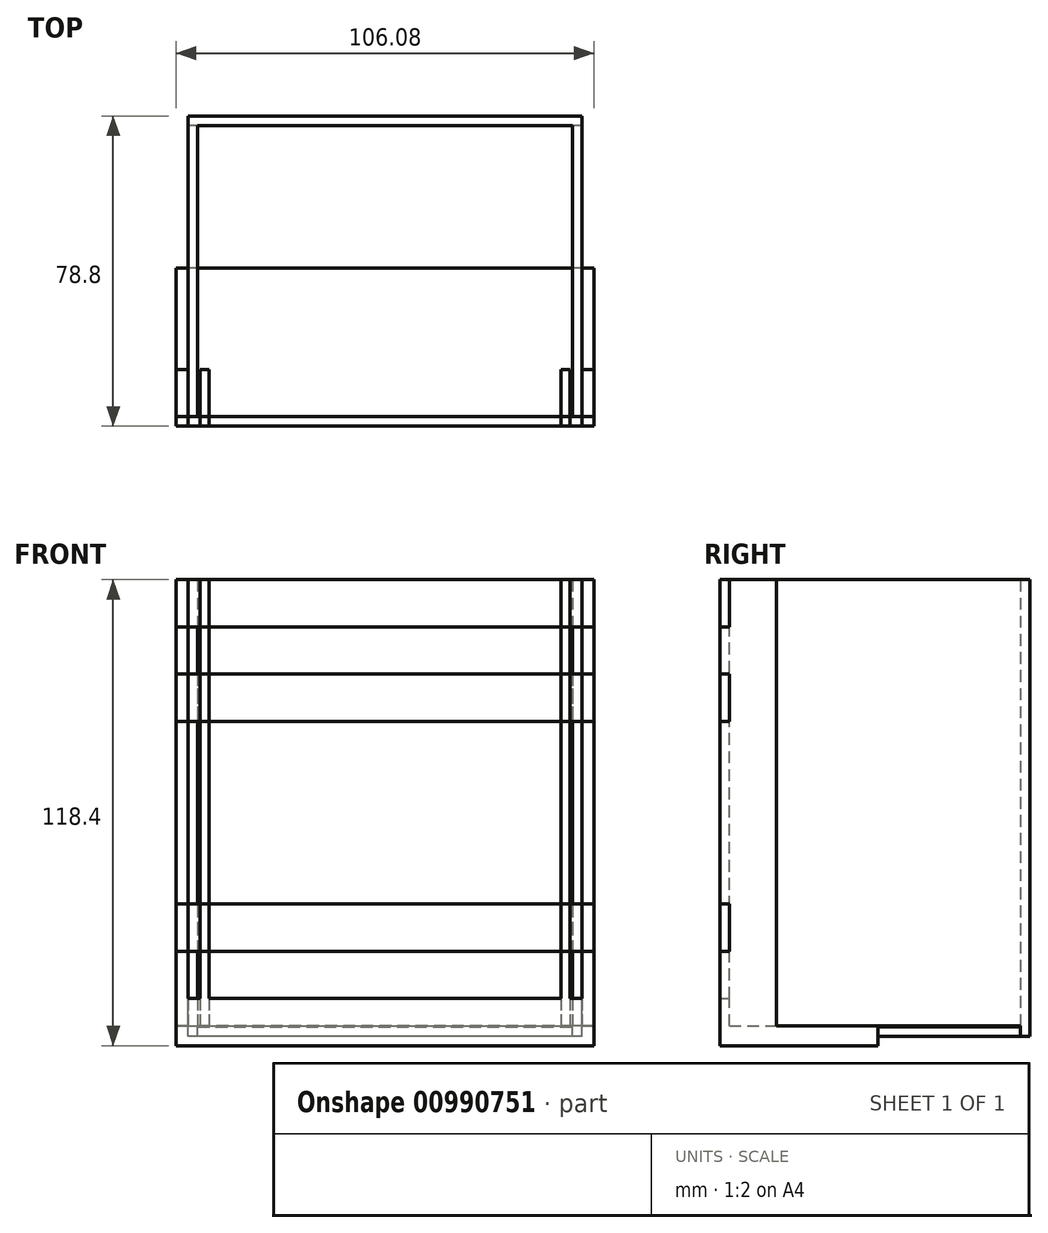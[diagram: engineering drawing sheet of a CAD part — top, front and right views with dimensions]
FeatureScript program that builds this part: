
annotation { "Feature Type Name" : "Feature", "Feature Type Description" : "" }
export const myFeature = defineFeature(function(context is Context, id is Id, definition is map)
    precondition{}
    {
        {
            var Q0;
            Q0=qCreatedBy(makeId("Front.planeOp"),FACE);
            var sketch = newSketch(context, id + "F0", { "sketchPlane" : qUnion([Q0])});
            skLineSegment(sketch, "E0.bottom", {"start": v(50, 0) * mm, "end": v(-50, 0) * mm});
            skLineSegment(sketch, "E0.top", {"start": v(50, 116) * mm, "end": v(-50, 116) * mm});
            skLineSegment(sketch, "E0.left", {"start": v(50, 0) * mm, "end": v(50, 116) * mm});
            skLineSegment(sketch, "E0.right", {"start": v(-50, 0) * mm, "end": v(-50, 116) * mm});
            skPoint(sketch, "E0.middle", {"position": v(0, 58) * mm});
            skSolve(sketch);
        }
        {
            var Q0;
            Q0 = qSketchRegion(id + "F0", true);
            extrude(context, id + "F1", {"entities" : qUnion([Q0]), "oppositeDirection" : true, "depth" : 2.4 * mm, "offsetDistance" : 25 * mm});
        }
        {
            var Q0;
            Q0=makeQuery(id+"F1.opExtrude","CAP_FACE",FACE,{"disambiguationData":[OSD([sQuery(id+"F0.wireOp",EDGE,"E0.bottom"),sQuery(id+"F0.wireOp",EDGE,"E0.top"),sQuery(id+"F0.wireOp",EDGE,"E0.left"),sQuery(id+"F0.wireOp",EDGE,"E0.right")])],"isStart":true});
            var sketch = newSketch(context, id + "F2", { "sketchPlane" : qUnion([Q0])});
            skLineSegment(sketch, "E1.bottom", {"start": v(-50, 116) * mm, "end": v(-47.6, 116) * mm});
            skLineSegment(sketch, "E1.top", {"start": v(-50, 2.6) * mm, "end": v(-47.6, 2.6) * mm});
            skLineSegment(sketch, "E1.left", {"start": v(-50, 116) * mm, "end": v(-50, 2.6) * mm});
            skLineSegment(sketch, "E1.right", {"start": v(-47.6, 116) * mm, "end": v(-47.6, 2.6) * mm});
            skLineSegment(sketch, "E2.bottom", {"start": v(50, 116) * mm, "end": v(47.6, 116) * mm});
            skLineSegment(sketch, "E2.top", {"start": v(50, 2.6) * mm, "end": v(47.6, 2.6) * mm});
            skLineSegment(sketch, "E2.left", {"start": v(50, 116) * mm, "end": v(50, 2.6) * mm});
            skLineSegment(sketch, "E2.right", {"start": v(47.6, 116) * mm, "end": v(47.6, 2.6) * mm});
            skSolve(sketch);
        }
        {
            var Q0;
            Q0 = qSketchRegion(id + "F2", true);
            extrude(context, id + "F3", {"entities" : qUnion([Q0]), "operationType" : NewBodyOperationType.ADD, "depth" : 74 * mm, "offsetDistance" : 25 * mm});
        }
        {
            var Q0;
            Q0=makeQuery(id+"F1.opExtrude","CAP_FACE",FACE,{"disambiguationData":[OSD([sQuery(id+"F0.wireOp",EDGE,"E0.bottom"),sQuery(id+"F0.wireOp",EDGE,"E0.top"),sQuery(id+"F0.wireOp",EDGE,"E0.left"),sQuery(id+"F0.wireOp",EDGE,"E0.right")])],"isStart":true});
            var sketch = newSketch(context, id + "F4", { "sketchPlane" : qUnion([Q0])});
            skLineSegment(sketch, "E3.bottom", {"start": v(-47.6, 0) * mm, "end": v(47.6, 0) * mm});
            skLineSegment(sketch, "E3.top", {"start": v(-47.6, 2.4) * mm, "end": v(47.6, 2.4) * mm});
            skLineSegment(sketch, "E3.left", {"start": v(-47.6, 0) * mm, "end": v(-47.6, 2.4) * mm});
            skLineSegment(sketch, "E3.right", {"start": v(47.6, 0) * mm, "end": v(47.6, 2.4) * mm});
            skSolve(sketch);
        }
        {
            var Q0;
            Q0 = qSketchRegion(id + "F4", true);
            extrude(context, id + "F5", {"entities" : qUnion([Q0]), "operationType" : NewBodyOperationType.ADD, "depth" : 36.25 * mm, "offsetDistance" : 25 * mm});
        }
        {
            var Q0;
            Q0=makeQuery(id+"F3.opExtrude","CAP_FACE",FACE,{"disambiguationData":[OSD([sQuery(id+"F2.wireOp",EDGE,"E1.bottom"),sQuery(id+"F2.wireOp",EDGE,"E1.top"),sQuery(id+"F2.wireOp",EDGE,"E1.left"),sQuery(id+"F2.wireOp",EDGE,"E1.right")])],"isStart":false});
            var sketch = newSketch(context, id + "F6", { "sketchPlane" : qUnion([Q0])});
            skLineSegment(sketch, "E4.bottom", {"start": v(53.04, 116) * mm, "end": v(-53.04, 116) * mm});
            skLineSegment(sketch, "E4.top", {"start": v(53.04, 104) * mm, "end": v(-53.04, 104) * mm});
            skLineSegment(sketch, "E4.left", {"start": v(53.04, 116) * mm, "end": v(53.04, 104) * mm});
            skPoint(sketch, "E4.middle", {"position": v(0, 110) * mm});
            skLineSegment(sketch, "E5.bottom", {"start": v(53.04, 92) * mm, "end": v(-53.04, 92) * mm});
            skLineSegment(sketch, "E5.top", {"start": v(53.04, 80) * mm, "end": v(-53.04, 80) * mm});
            skLineSegment(sketch, "E5.left", {"start": v(53.04, 92) * mm, "end": v(53.04, 80) * mm});
            skLineSegment(sketch, "E5.right", {"start": v(-53.04, 92) * mm, "end": v(-53.04, 80) * mm});
            skPoint(sketch, "E5.middle", {"position": v(0, 86) * mm});
            skLineSegment(sketch, "E6.bottom", {"start": v(53.04, 9.6) * mm, "end": v(-53.04, 9.6) * mm});
            skLineSegment(sketch, "E6.top", {"start": v(53.04, -2.4) * mm, "end": v(-53.04, -2.4) * mm});
            skLineSegment(sketch, "E6.left", {"start": v(53.04, 9.6) * mm, "end": v(53.04, -2.4) * mm});
            skLineSegment(sketch, "E6.right", {"start": v(-53.04, 9.6) * mm, "end": v(-53.04, -2.4) * mm});
            skPoint(sketch, "E6.middle", {"position": v(0, 3.6) * mm});
            skLineSegment(sketch, "E7.bottom", {"start": v(53.04, 33.6) * mm, "end": v(-53.04, 33.6) * mm});
            skLineSegment(sketch, "E7.top", {"start": v(53.04, 21.6) * mm, "end": v(-53.04, 21.6) * mm});
            skLineSegment(sketch, "E7.left", {"start": v(53.04, 33.6) * mm, "end": v(53.04, 21.6) * mm});
            skLineSegment(sketch, "E7.right", {"start": v(-53.04, 33.6) * mm, "end": v(-53.04, 21.6) * mm});
            skPoint(sketch, "E7.middle", {"position": v(0, 27.6) * mm});
            skLineSegment(sketch, "E8", {"start": v(-53.04, 116) * mm, "end": v(-53.04, 104) * mm});
            skSolve(sketch);
        }
        {
            var Q0;
            Q0 = qSketchRegion(id + "F6", true);
            extrude(context, id + "F7", {"entities" : qUnion([Q0]), "depth" : 2.4 * mm, "offsetDistance" : 25 * mm});
        }
        {
            var Q0;
            Q0=makeQuery(id+"F3.opExtrude","CAP_FACE",FACE,{"disambiguationData":[OSD([sQuery(id+"F2.wireOp",EDGE,"E2.bottom"),sQuery(id+"F2.wireOp",EDGE,"E2.top"),sQuery(id+"F2.wireOp",EDGE,"E2.left"),sQuery(id+"F2.wireOp",EDGE,"E2.right")])],"isStart":false});
            var sketch = newSketch(context, id + "F8", { "sketchPlane" : qUnion([Q0])});
            skLineSegment(sketch, "E9.bottom", {"start": v(53.04, 116) * mm, "end": v(50.04, 116) * mm});
            skLineSegment(sketch, "E9.top", {"start": v(53.04, -2.4) * mm, "end": v(50.04, -2.4) * mm});
            skLineSegment(sketch, "E9.left", {"start": v(53.04, 116) * mm, "end": v(53.04, -2.4) * mm});
            skLineSegment(sketch, "E9.right", {"start": v(50.04, 116) * mm, "end": v(50.04, -2.4) * mm});
            skLineSegment(sketch, "E10.bottom", {"start": v(-50.04, 116) * mm, "end": v(-53.04, 116) * mm});
            skLineSegment(sketch, "E10.top", {"start": v(-50.04, -2.4) * mm, "end": v(-53.04, -2.4) * mm});
            skLineSegment(sketch, "E10.left", {"start": v(-50.04, 116) * mm, "end": v(-50.04, -2.4) * mm});
            skLineSegment(sketch, "E10.right", {"start": v(-53.04, 116) * mm, "end": v(-53.04, -2.4) * mm});
            skLineSegment(sketch, "E11.bottom", {"start": v(47.04, 116) * mm, "end": v(44.64, 116) * mm});
            skLineSegment(sketch, "E11.top", {"start": v(47.04, 2.6) * mm, "end": v(44.64, 2.6) * mm});
            skLineSegment(sketch, "E11.left", {"start": v(47.04, 116) * mm, "end": v(47.04, 2.6) * mm});
            skLineSegment(sketch, "E11.right", {"start": v(44.64, 116) * mm, "end": v(44.64, 2.6) * mm});
            skLineSegment(sketch, "E12.bottom", {"start": v(-47.04, 116) * mm, "end": v(-44.64, 116) * mm});
            skLineSegment(sketch, "E12.top", {"start": v(-47.04, 2.6) * mm, "end": v(-44.64, 2.6) * mm});
            skLineSegment(sketch, "E12.left", {"start": v(-47.04, 116) * mm, "end": v(-47.04, 2.6) * mm});
            skLineSegment(sketch, "E12.right", {"start": v(-44.64, 116) * mm, "end": v(-44.64, 2.6) * mm});
            skSolve(sketch);
        }
        {
            var Q0;
            Q0 = qSketchRegion(id + "F8", true);
            var Q1;
            Q1=makeQuery(id+"F7.opExtrude","CAP_FACE",FACE,{"disambiguationData":[OSD([sQuery(id+"F6.wireOp",EDGE,"E6.bottom"),sQuery(id+"F6.wireOp",EDGE,"E6.top"),sQuery(id+"F6.wireOp",EDGE,"E6.left"),sQuery(id+"F6.wireOp",EDGE,"E6.right")])],"isStart":false});
            extrude(context, id + "F9", {"entities" : qUnion([Q0]), "oppositeDirection" : true, "depth" : 12 * mm, "offsetDistance" : 25 * mm, "hasSecondDirection" : true, "secondDirectionBound" : SecondDirectionBoundingType.UP_TO_SURFACE, "secondDirectionOppositeDirection" : false, "secondDirectionDepth" : 2.4 * mm, "secondDirectionBoundEntityFace" : qUnion([Q1])});
        }
        {
            var Q0;
            Q0=makeQuery(id+"F6.imprint","IMPRINT",FACE,{"disambiguationData":[TD([[makeQuery(id+"F6.imprint","IMPRINT",EDGE,{"derivedFrom":sQuery(id+"F6.wireOp",EDGE,"E6.top")}),-1.0]])]});
            var sketch = newSketch(context, id + "F10", { "sketchPlane" : qUnion([Q0])});
            skLineSegment(sketch, "E13.bottom", {"start": v(-53.04, 2.6) * mm, "end": v(53.04, 2.6) * mm});
            skLineSegment(sketch, "E13.top", {"start": v(-53.04, -2.4) * mm, "end": v(53.04, -2.4) * mm});
            skLineSegment(sketch, "E13.left", {"start": v(-53.04, 2.6) * mm, "end": v(-53.04, -2.4) * mm});
            skLineSegment(sketch, "E13.right", {"start": v(53.04, 2.6) * mm, "end": v(53.04, -2.4) * mm});
            skPoint(sketch, "E13.middle", {"position": v(0, 0.1) * mm});
            skSolve(sketch);
        }
        {
            var Q0;
            Q0 = qSketchRegion(id + "F10", true);
            var Q1;
            Q1=makeQuery(id+"F5.opExtrude","CAP_FACE",FACE,{"disambiguationData":[OSD([sQuery(id+"F4.wireOp",EDGE,"E3.bottom"),sQuery(id+"F4.wireOp",EDGE,"E3.top"),sQuery(id+"F4.wireOp",EDGE,"E3.left"),sQuery(id+"F4.wireOp",EDGE,"E3.right")])],"isStart":false});
            extrude(context, id + "F11", {"entities" : qUnion([Q0]), "operationType" : NewBodyOperationType.ADD, "endBound" : BoundingType.UP_TO_SURFACE, "oppositeDirection" : true, "depth" : 25 * mm, "endBoundEntityFace" : qUnion([Q1]), "offsetDistance" : 25 * mm});
        }
    });
